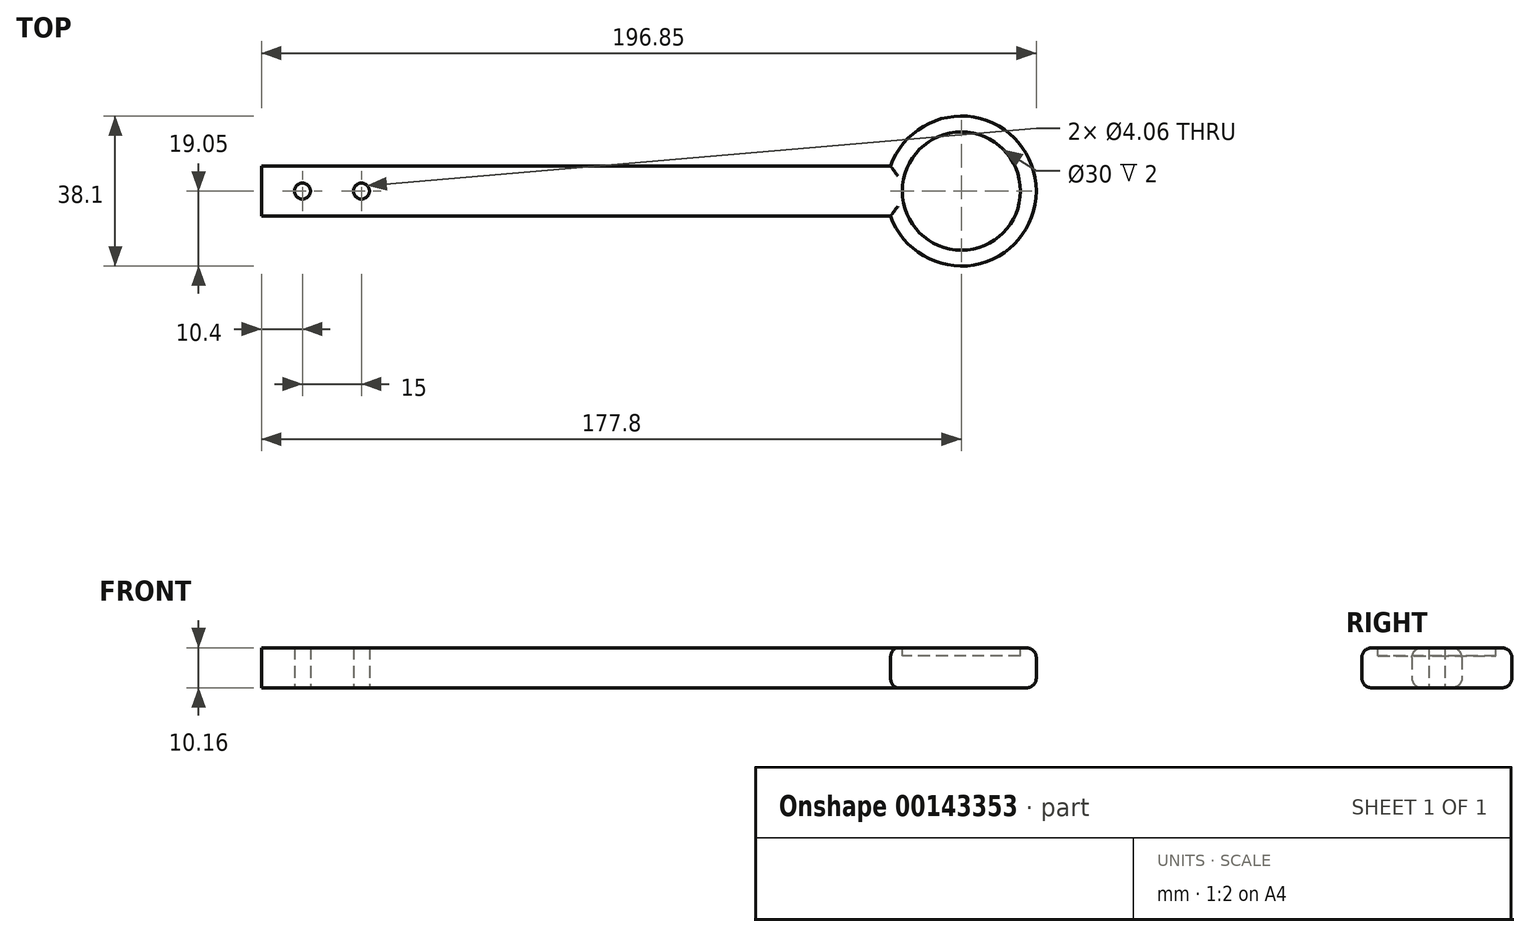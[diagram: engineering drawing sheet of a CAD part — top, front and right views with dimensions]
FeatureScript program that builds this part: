
annotation { "Feature Type Name" : "Feature", "Feature Type Description" : "" }
export const myFeature = defineFeature(function(context is Context, id is Id, definition is map)
    precondition{}
    {
        {
            var Q0;
            Q0=qCreatedBy(makeId("Top.planeOp"),FACE);
            var sketch = newSketch(context, id + "F0", { "sketchPlane" : qUnion([Q0])});
            skLineSegment(sketch, "E0.bottom", {"start": v(-88.9, 6.35) * mm, "end": v(88.9, 6.35) * mm});
            skLineSegment(sketch, "E0.top", {"start": v(-88.9, -6.35) * mm, "end": v(88.9, -6.35) * mm});
            skLineSegment(sketch, "E0.left", {"start": v(-88.9, 6.35) * mm, "end": v(-88.9, -6.35) * mm});
            skLineSegment(sketch, "E0.right", {"start": v(88.9, 6.35) * mm, "end": v(88.9, -6.35) * mm});
            skPoint(sketch, "E0.middle", {"position": v(0, 0) * mm});
            skCircle(sketch, "E1", {"center": v(88.9, 0) * mm, "radius": 19.05 * mm});
            skLineSegment(sketch, "E2", {"start": v(-88.9, 0) * mm, "end": v(-63.5, 0) * mm});
            skPoint(sketch, "E2.endSnap0", {"position": v(-88.9, 0) * mm});
            skCircle(sketch, "E3", {"center": v(-63.5, 0) * mm, "radius": 2.03 * mm});
            skLineSegment(sketch, "E4", {"start": v(-45.8, -6.35) * mm, "end": v(-45.8, 6.35) * mm});
            skCircle(sketch, "E5", {"center": v(-78.5, 0) * mm, "radius": 2.03 * mm});
            skSolve(sketch);
        }
        {
            var Q0;
            {var subQ0=sQuery(id+"F0.wireOp",EDGE,"E0.right");Q0=makeQuery(id+"F0.imprint","IMPRINT",FACE,{"disambiguationData":[TD([[makeQuery(id+"F0.imprint","IMPRINT",EDGE,{"derivedFrom":subQ0}),-1.0]])]});}
            var Q1;
            {var subQ0=sQuery(id+"F0.wireOp",EDGE,"E4");Q1=makeQuery(id+"F0.imprint","IMPRINT",FACE,{"disambiguationData":[TD([[makeQuery(id+"F0.imprint","IMPRINT",EDGE,{"derivedFrom":subQ0}),-1.0]])]});}
            var Q2;
            Q2=makeQuery(id+"F0.imprint","IMPRINT",FACE,{"disambiguationData":[TD([[makeQuery(id+"F0.imprint","IMPRINT",EDGE,{"derivedFrom":sQuery(id+"F0.wireOp",EDGE,"E3")}),-1.0]])]});
            var Q3;
            {var subQ0=sQuery(id+"F0.wireOp",EDGE,"E0.right");Q3=makeQuery(id+"F0.imprint","IMPRINT",FACE,{"disambiguationData":[TD([[makeQuery(id+"F0.imprint","IMPRINT",EDGE,{"derivedFrom":subQ0}),1.0]])]});}
            extrude(context, id + "F1", {"entities" : qUnion([Q0, Q1, Q2, Q3]), "depth" : 10.16 * mm});
        }
        {
            var Q0;
            Q0=makeQuery(id+"F1.opExtrude","CAP_EDGE",EDGE,{"disambiguationData":[OSD([sQuery(id+"F0.wireOp",EDGE,"E1")])],"isStart":false});
            var Q1;
            Q1=makeQuery(id+"F1.opExtrude","CAP_EDGE",EDGE,{"disambiguationData":[OSD([sQuery(id+"F0.wireOp",EDGE,"E0.bottom")])],"isStart":false});
            var Q2;
            Q2=makeQuery(id+"F1.opExtrude","CAP_EDGE",EDGE,{"disambiguationData":[OSD([sQuery(id+"F0.wireOp",EDGE,"E0.top")])],"isStart":false});
            var Q3;
            Q3=makeQuery(id+"F1.opExtrude","CAP_EDGE",EDGE,{"disambiguationData":[OSD([sQuery(id+"F0.wireOp",EDGE,"E0.bottom")])],"isStart":true});
            var Q4;
            Q4=makeQuery(id+"F1.opExtrude","CAP_EDGE",EDGE,{"disambiguationData":[OSD([sQuery(id+"F0.wireOp",EDGE,"E0.top")])],"isStart":true});
            var Q5;
            Q5=makeQuery(id+"F1.opExtrude","CAP_EDGE",EDGE,{"disambiguationData":[OSD([sQuery(id+"F0.wireOp",EDGE,"E1")])],"isStart":true});
            fillet(context, id + "F2", {"entities" : qUnion([Q0, Q1, Q2, Q3, Q4, Q5]), "radius" : 2.5 * mm, "tangentPropagation" : true, "allowEdgeOverflow" : false});
        }
        {
            var Q0;
            Q0=makeQuery(id+"F2.opFillet","SPLIT",FACE,{"disambiguationData":[OD(1.0)],"derivedFrom":makeQuery(id+"F1.opExtrude","CAP_FACE",FACE,{"disambiguationData":[OSD([sQuery(id+"F0.wireOp",EDGE,"E0.bottom"),sQuery(id+"F0.wireOp",EDGE,"E0.top"),sQuery(id+"F0.wireOp",EDGE,"E0.left"),sQuery(id+"F0.wireOp",EDGE,"E1"),sQuery(id+"F0.wireOp",EDGE,"E3")])],"isStart":false})});
            var sketch = newSketch(context, id + "F3", { "sketchPlane" : qUnion([Q0])});
            skCircle(sketch, "E6", {"center": v(88.9, 0) * mm, "radius": 15 * mm});
            skSolve(sketch);
        }
        {
            var Q0;
            Q0=makeQuery(id+"F3.imprint","IMPRINT",FACE,{"disambiguationData":[TD([[makeQuery(id+"F3.imprint","IMPRINT",EDGE,{"derivedFrom":sQuery(id+"F3.wireOp",EDGE,"E6")}),1.0]])]});
            extrude(context, id + "F4", {"entities" : qUnion([Q0]), "operationType" : NewBodyOperationType.REMOVE, "oppositeDirection" : true, "depth" : 2 * mm});
        }
    });
